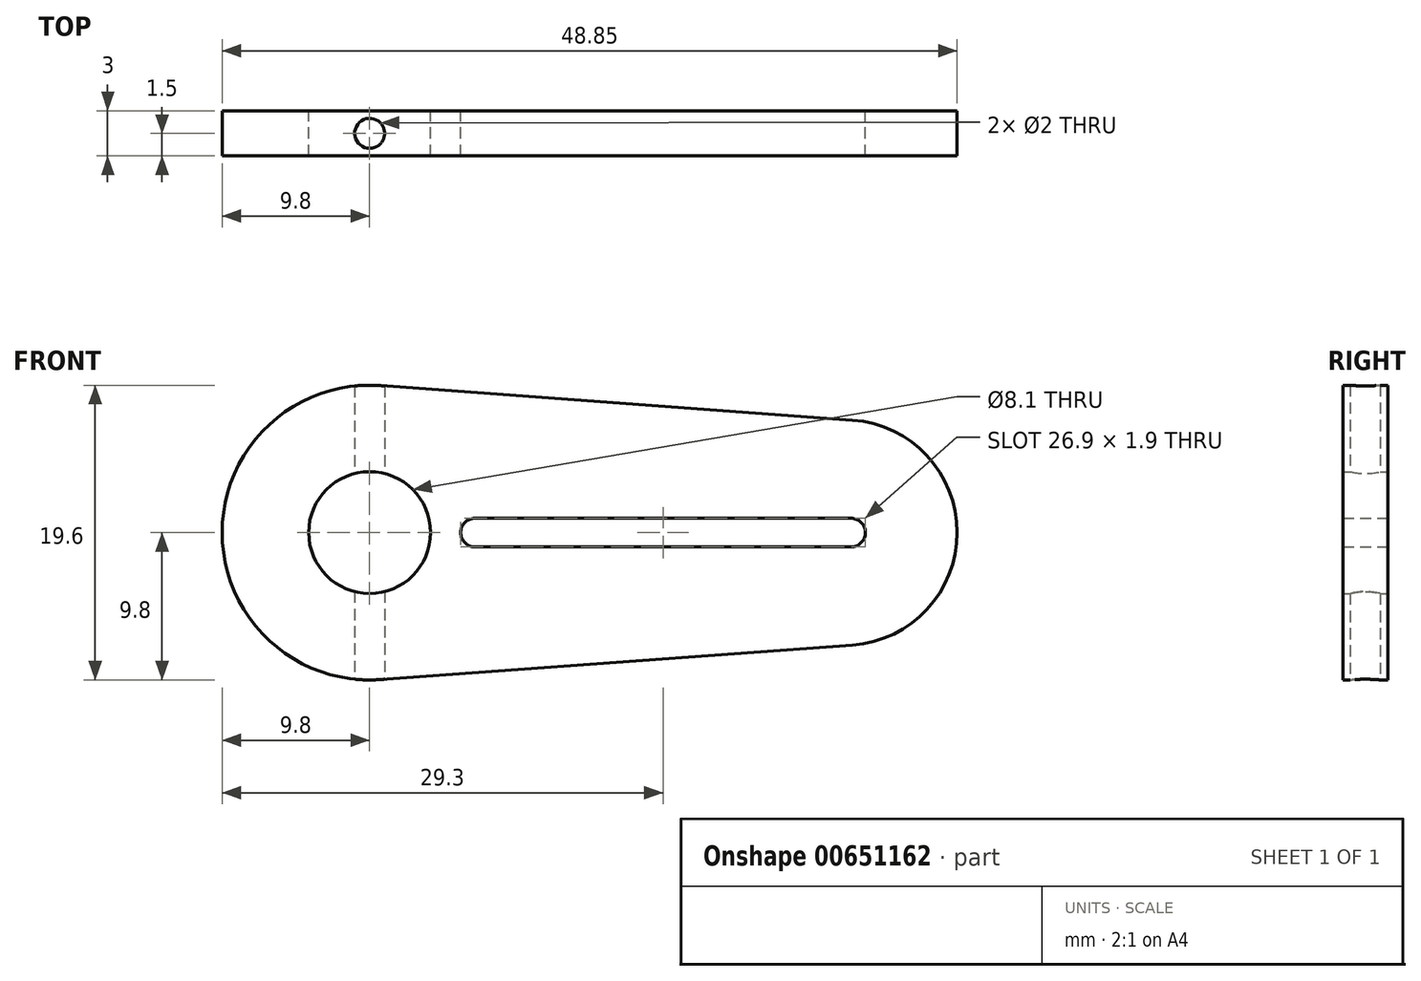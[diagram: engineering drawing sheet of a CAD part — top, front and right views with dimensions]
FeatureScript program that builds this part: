
annotation { "Feature Type Name" : "Feature", "Feature Type Description" : "" }
export const myFeature = defineFeature(function(context is Context, id is Id, definition is map)
    precondition{}
    {
        {
            var Q0;
            Q0=qCreatedBy(makeId("Front.planeOp"),FACE);
            var sketch = newSketch(context, id + "F0", { "sketchPlane" : qUnion([Q0])});
            skCircle(sketch, "E0", {"center": v(0, 0) * mm, "radius": 4.05 * mm});
            skLineSegment(sketch, "E1", {"start": v(4.05, -9.53) * mm, "end": v(4.05, 11.18) * mm, "construction": true});
            skArc(sketch, "E2", {"start": v(32.1, -7.48) * mm, "mid": v(39.05, 0) * mm, "end": v(32.1, 7.48) * mm});
            skLineSegment(sketch, "E3", {"start": v(0.71, 9.77) * mm, "end": v(32.1, 7.48) * mm});
            skLineSegment(sketch, "E4", {"start": v(0, 0) * mm, "end": v(-19.82, 0) * mm, "construction": true});
            skArc(sketch, "E5", {"start": v(0.71, 9.77) * mm, "mid": v(-9.8, 0) * mm, "end": v(0.71, -9.77) * mm});
            skLineSegment(sketch, "E6.MirrorCS", {"start": v(0.71, -9.77) * mm, "end": v(32.1, -7.48) * mm});
            skPoint(sketch, "E7.orphan", {"position": v(4.05, 0) * mm});
            skPoint(sketch, "E8.orphan", {"position": v(4.05, 9.53) * mm});
            skLineSegment(sketch, "E9", {"start": v(0, 0) * mm, "end": v(48.13, 0) * mm, "construction": true});
            skArc(sketch, "E10", {"start": v(32, -0.95) * mm, "mid": v(32.95, 0) * mm, "end": v(32, 0.95) * mm});
            skArc(sketch, "E11", {"start": v(7, 0.95) * mm, "mid": v(6.05, 0) * mm, "end": v(7, -0.95) * mm});
            skLineSegment(sketch, "E12", {"start": v(7, 0.95) * mm, "end": v(32, 0.95) * mm});
            skLineSegment(sketch, "E13", {"start": v(7, -0.95) * mm, "end": v(32, -0.95) * mm});
            skSolve(sketch);
        }
        {
            var Q0;
            Q0 = qSketchRegion(id + "F0", true);
            extrude(context, id + "F1", {"entities" : qUnion([Q0]), "endBound" : BoundingType.SYMMETRIC, "depth" : 3 * mm, "offsetDistance" : 25 * mm});
        }
        {
            var Q0;
            Q0=qCreatedBy(makeId("Top.planeOp"),FACE);
            var sketch = newSketch(context, id + "F2", { "sketchPlane" : qUnion([Q0])});
            skCircle(sketch, "E14", {"center": v(0, 0) * mm, "radius": 1 * mm});
            skSolve(sketch);
        }
        {
            var Q0;
            Q0 = qSketchRegion(id + "F2", true);
            extrude(context, id + "F3", {"entities" : qUnion([Q0]), "operationType" : NewBodyOperationType.REMOVE, "endBound" : BoundingType.SYMMETRIC, "depth" : 25 * mm, "offsetDistance" : 25 * mm});
        }
    });
